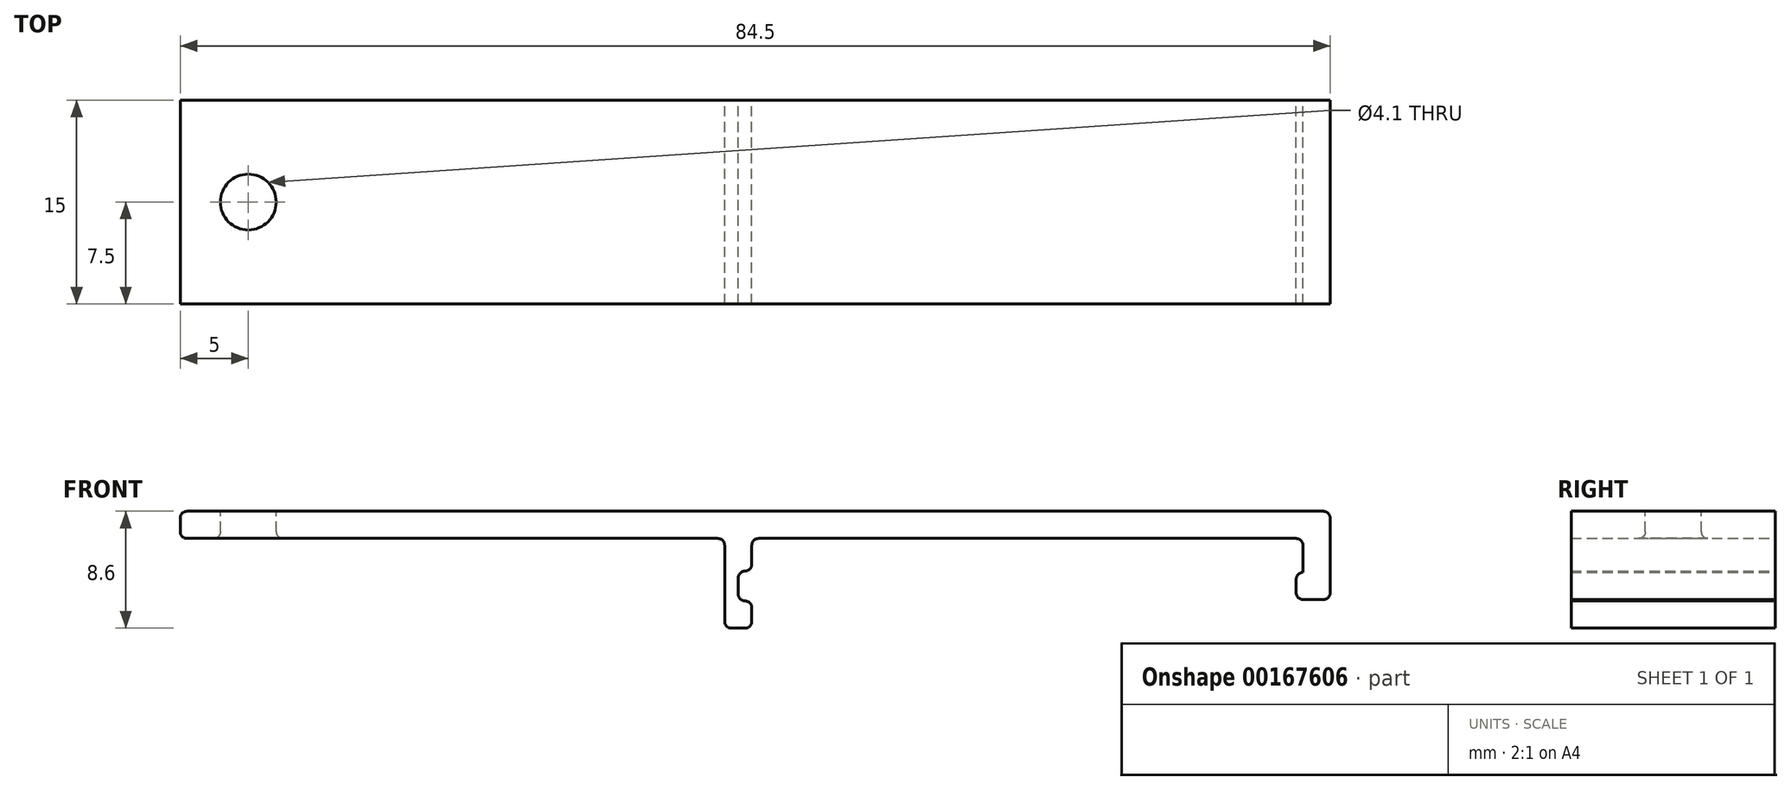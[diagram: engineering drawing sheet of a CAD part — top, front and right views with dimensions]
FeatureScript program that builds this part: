
annotation { "Feature Type Name" : "Feature", "Feature Type Description" : "" }
export const myFeature = defineFeature(function(context is Context, id is Id, definition is map)
    precondition{}
    {
        {
            var Q0;
            Q0=qCreatedBy(makeId("Front.planeOp"),FACE);
            var sketch = newSketch(context, id + "F0", { "sketchPlane" : qUnion([Q0])});
            skLineSegment(sketch, "E0.bottom", {"start": v(-42.25, 0) * mm, "end": v(42.25, 0) * mm});
            skLineSegment(sketch, "E0.top", {"start": v(-42.25, -2) * mm, "end": v(42.25, -2) * mm});
            skLineSegment(sketch, "E0.left", {"start": v(-42.25, 0) * mm, "end": v(-42.25, -2) * mm});
            skLineSegment(sketch, "E0.right", {"start": v(42.25, 0) * mm, "end": v(42.25, -2) * mm});
            skLineSegment(sketch, "E1", {"start": v(-2.25, -2) * mm, "end": v(-2.25, -8.6) * mm});
            skLineSegment(sketch, "E2", {"start": v(-2.25, -8.6) * mm, "end": v(-0.25, -8.6) * mm});
            skLineSegment(sketch, "E3", {"start": v(-0.25, -8.6) * mm, "end": v(-0.25, -6.6) * mm});
            skLineSegment(sketch, "E4", {"start": v(-0.25, -6.6) * mm, "end": v(-1.25, -6.6) * mm});
            skLineSegment(sketch, "E5", {"start": v(-1.25, -6.6) * mm, "end": v(-1.25, -4.4) * mm});
            skLineSegment(sketch, "E6", {"start": v(-1.25, -4.4) * mm, "end": v(-0.25, -4.4) * mm});
            skLineSegment(sketch, "E7", {"start": v(-0.25, -4.4) * mm, "end": v(-0.25, -2) * mm});
            skLineSegment(sketch, "E8", {"start": v(42.25, -2) * mm, "end": v(42.25, -6.5) * mm});
            skLineSegment(sketch, "E9", {"start": v(42.25, -6.5) * mm, "end": v(39.75, -6.5) * mm});
            skLineSegment(sketch, "E10", {"start": v(39.75, -6.5) * mm, "end": v(39.75, -4.5) * mm});
            skLineSegment(sketch, "E11", {"start": v(39.75, -4.5) * mm, "end": v(40.25, -4.5) * mm});
            skLineSegment(sketch, "E12", {"start": v(40.25, -4.5) * mm, "end": v(40.25, -2) * mm});
            skSolve(sketch);
        }
        {
            var Q0;
            {var subQ0=sQuery(id+"F0.wireOp",EDGE,"E1");Q0=makeQuery(id+"F0.imprint","IMPRINT",FACE,{"disambiguationData":[TD([[makeQuery(id+"F0.imprint","IMPRINT",EDGE,{"derivedFrom":subQ0}),1.0]])]});}
            var Q1;
            Q1=makeQuery(id+"F0.imprint","IMPRINT",FACE,{"disambiguationData":[TD([[makeQuery(id+"F0.imprint","IMPRINT",EDGE,{"derivedFrom":sQuery(id+"F0.wireOp",EDGE,"E0.bottom")}),-1.0]])]});
            var Q2;
            {var subQ0=sQuery(id+"F0.wireOp",EDGE,"E8");Q2=makeQuery(id+"F0.imprint","IMPRINT",FACE,{"disambiguationData":[TD([[makeQuery(id+"F0.imprint","IMPRINT",EDGE,{"derivedFrom":subQ0}),-1.0]])]});}
            extrude(context, id + "F1", {"entities" : qUnion([Q0, Q1, Q2]), "depth" : 15 * mm});
        }
        {
            var Q0;
            Q0=makeQuery(id+"F1.opExtrude","SWEPT_FACE",FACE,{"disambiguationData":[OSD([sQuery(id+"F0.wireOp",EDGE,"E0.bottom")])]});
            var sketch = newSketch(context, id + "F2", { "sketchPlane" : qUnion([Q0])});
            skCircle(sketch, "E13", {"center": v(-37.25, -7.5) * mm, "radius": 2.05 * mm});
            skSolve(sketch);
        }
        {
            var Q0;
            Q0=makeQuery(id+"F2.imprint","IMPRINT",FACE,{"disambiguationData":[TD([[makeQuery(id+"F2.imprint","IMPRINT",EDGE,{"derivedFrom":sQuery(id+"F2.wireOp",EDGE,"E13")}),1.0]])]});
            extrude(context, id + "F3", {"entities" : qUnion([Q0]), "operationType" : NewBodyOperationType.REMOVE, "oppositeDirection" : true, "depth" : 25 * mm});
        }
        {
            var Q0;
            Q0=makeQuery(id+"F1.opExtrude","SWEPT_EDGE",EDGE,{"disambiguationData":[OSD([sQuery(id+"F0.wireOp",EDGE,"E4"),sQuery(id+"F0.wireOp",EDGE,"E5")])]});
            var Q1;
            Q1=makeQuery(id+"F1.opExtrude","SWEPT_EDGE",EDGE,{"disambiguationData":[OSD([sQuery(id+"F0.wireOp",EDGE,"E2"),sQuery(id+"F0.wireOp",EDGE,"E3")])]});
            var Q2;
            Q2=makeQuery(id+"F1.opExtrude","SWEPT_EDGE",EDGE,{"disambiguationData":[OSD([sQuery(id+"F0.wireOp",EDGE,"E9"),sQuery(id+"F0.wireOp",EDGE,"E10")])]});
            var Q3;
            Q3=makeQuery(id+"F1.opExtrude","SWEPT_EDGE",EDGE,{"disambiguationData":[OSD([sQuery(id+"F0.wireOp",EDGE,"E10"),sQuery(id+"F0.wireOp",EDGE,"E11")])]});
            var Q4;
            Q4=makeQuery(id+"F3.boolean.opBoolean","COPY",EDGE,{"derivedFrom":makeQuery(id+"F3.opExtrude","CAP_EDGE",EDGE,{"disambiguationData":[OSD([sQuery(id+"F2.wireOp",EDGE,"E13")])],"isStart":true})});
            var Q5;
            Q5=makeQuery(id+"F1.opExtrude","SWEPT_EDGE",EDGE,{"disambiguationData":[OSD([sQuery(id+"F0.wireOp",EDGE,"E0.bottom"),sQuery(id+"F0.wireOp",EDGE,"E0.right")])]});
            var Q6;
            Q6=makeQuery(id+"F1.opExtrude","SWEPT_EDGE",EDGE,{"disambiguationData":[OSD([sQuery(id+"F0.wireOp",EDGE,"E8"),sQuery(id+"F0.wireOp",EDGE,"E9")])]});
            var Q7;
            Q7=makeQuery(id+"F1.opExtrude","SWEPT_EDGE",EDGE,{"disambiguationData":[OSD([sQuery(id+"F0.wireOp",EDGE,"E0.bottom"),sQuery(id+"F0.wireOp",EDGE,"E0.left")])]});
            var Q8;
            Q8=makeQuery(id+"F1.opExtrude","SWEPT_EDGE",EDGE,{"disambiguationData":[OSD([sQuery(id+"F0.wireOp",EDGE,"E0.top"),sQuery(id+"F0.wireOp",EDGE,"E0.left")])]});
            var Q9;
            Q9=makeQuery(id+"F1.opExtrude","SWEPT_EDGE",EDGE,{"disambiguationData":[OSD([sQuery(id+"F0.wireOp",EDGE,"E0.top"),sQuery(id+"F0.wireOp",EDGE,"E1")])]});
            var Q10;
            Q10=makeQuery(id+"F1.opExtrude","SWEPT_EDGE",EDGE,{"disambiguationData":[OSD([sQuery(id+"F0.wireOp",EDGE,"E0.top"),sQuery(id+"F0.wireOp",EDGE,"E7")])]});
            var Q11;
            Q11=makeQuery(id+"F1.opExtrude","SWEPT_EDGE",EDGE,{"disambiguationData":[OSD([sQuery(id+"F0.wireOp",EDGE,"E0.top"),sQuery(id+"F0.wireOp",EDGE,"E12")])]});
            var Q12;
            Q12=makeQuery(id+"F1.opExtrude","SWEPT_EDGE",EDGE,{"disambiguationData":[OSD([sQuery(id+"F0.wireOp",EDGE,"E1"),sQuery(id+"F0.wireOp",EDGE,"E2")])]});
            var Q13;
            {var subQ0=sQuery(id+"F0.wireOp",EDGE,"E0.top");Q13=makeQuery(id+"F3.boolean.opBoolean","INTERSECT",EDGE,{"derivedFrom":[makeQuery(id+"F1.opExtrude","SWEPT_FACE",FACE,{"disambiguationData":[OSD([subQ0]),TDD([makeQuery(id+"F0.imprint","IMPRINT",EDGE,{"disambiguationData":[TD([[makeQuery(id+"F0.imprint","INTERSECT",VERTEX,{"derivedFrom":[subQ0,sQuery(id+"F0.wireOp",EDGE,"E0.left")]}),-1.0]])],"derivedFrom":subQ0})])]}),makeQuery(id+"F3.opExtrude","SWEPT_FACE",FACE,{"disambiguationData":[OSD([sQuery(id+"F2.wireOp",EDGE,"E13")])]})]});}
            var Q14;
            Q14=makeQuery(id+"F1.opExtrude","SWEPT_EDGE",EDGE,{"disambiguationData":[OSD([sQuery(id+"F0.wireOp",EDGE,"E6"),sQuery(id+"F0.wireOp",EDGE,"E7")])]});
            var Q15;
            Q15=makeQuery(id+"F1.opExtrude","SWEPT_EDGE",EDGE,{"disambiguationData":[OSD([sQuery(id+"F0.wireOp",EDGE,"E5"),sQuery(id+"F0.wireOp",EDGE,"E6")])]});
            var Q16;
            Q16=makeQuery(id+"F1.opExtrude","SWEPT_EDGE",EDGE,{"disambiguationData":[OSD([sQuery(id+"F0.wireOp",EDGE,"E3"),sQuery(id+"F0.wireOp",EDGE,"E4")])]});
            fillet(context, id + "F4", {"entities" : qUnion([Q0, Q1, Q2, Q3, Q4, Q5, Q6, Q7, Q8, Q9, Q10, Q11, Q12, Q13, Q14, Q15, Q16]), "radius" : 0.5 * mm, "tangentPropagation" : true, "allowEdgeOverflow" : false});
        }
    });
